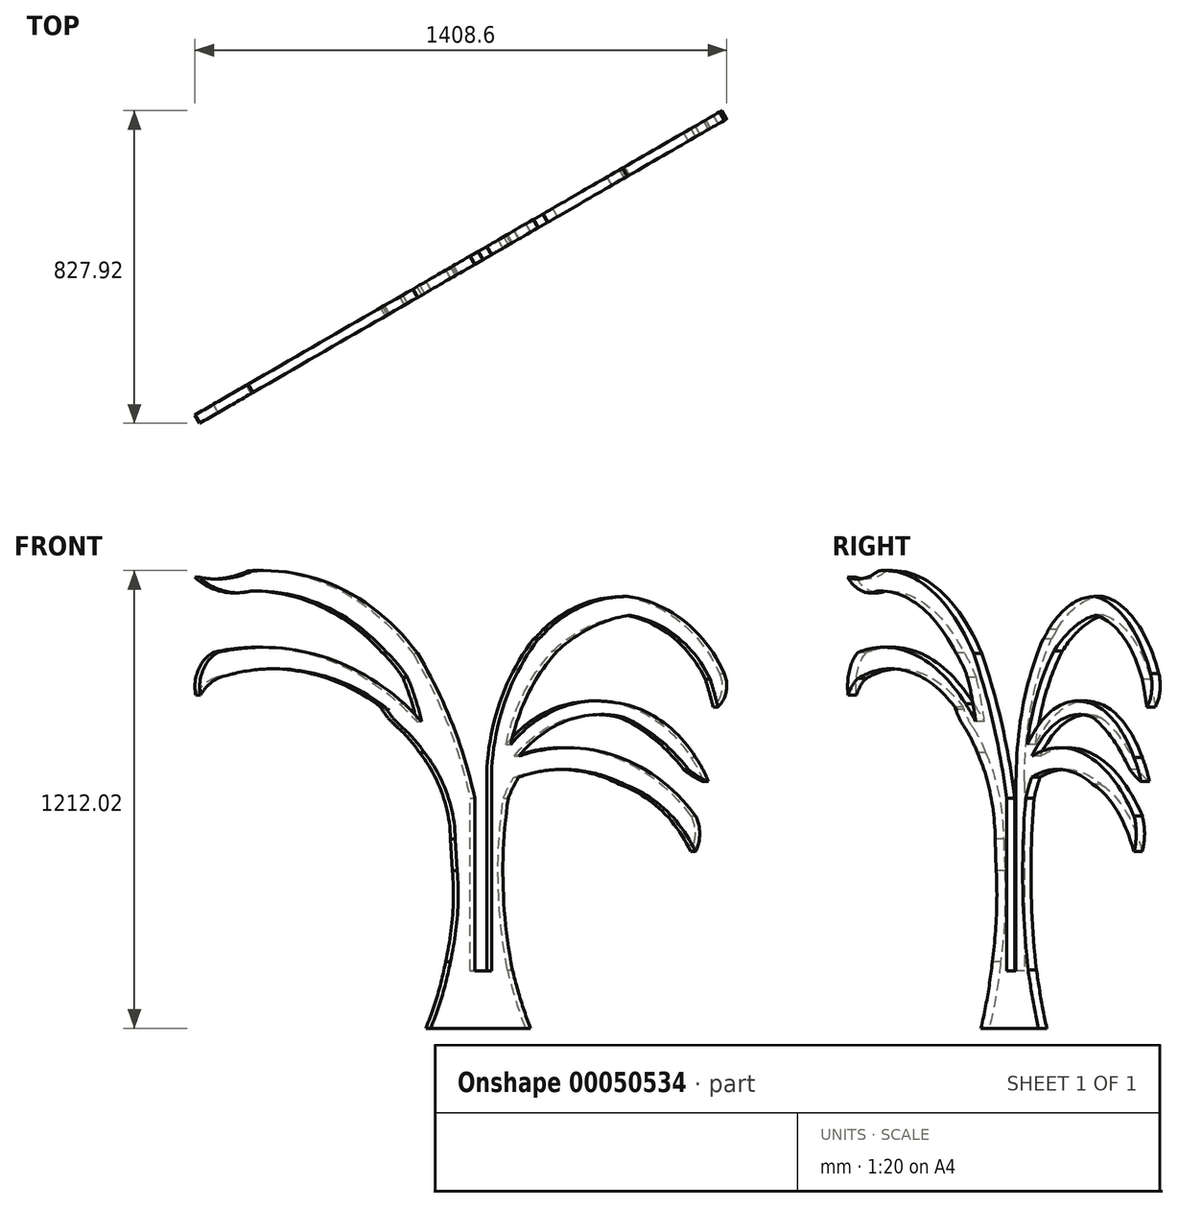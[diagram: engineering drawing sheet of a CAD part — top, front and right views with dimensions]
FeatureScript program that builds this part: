
annotation { "Feature Type Name" : "Feature", "Feature Type Description" : "" }
export const myFeature = defineFeature(function(context is Context, id is Id, definition is map)
    precondition{}
    {
        {
            var Q0;
            Q0=qCreatedBy(makeId("Front.planeOp"),FACE);
            var sketch = newSketch(context, id + "F0", { "sketchPlane" : qUnion([Q0])});
            skLineSegment(sketch, "E0", {"start": v(290.3, 214.33) * mm, "end": v(290.72, 214.4) * mm});
            skArc(sketch, "E1", {"start": v(291.68, 214.42) * mm, "mid": v(291, 214.37) * mm, "end": v(290.3, 214.33) * mm});
            skArc(sketch, "E2", {"start": v(250.18, 167.25) * mm, "mid": v(213.74, 135.77) * mm, "end": v(182.02, 99.53) * mm});
            skArc(sketch, "E3", {"start": v(290.72, 214.4) * mm, "mid": v(290.52, 214.37) * mm, "end": v(290.31, 214.33) * mm});
            skLineSegment(sketch, "E4", {"start": v(-55.85, -81.88) * mm, "end": v(-55.85, -83.32) * mm});
            skPoint(sketch, "E5.start.orphan", {"position": v(-34.4, -113.68) * mm});
            skPoint(sketch, "E6.orphan", {"position": v(111.38, -113.68) * mm});
            skArc(sketch, "E7", {"start": v(250.18, 167.25) * mm, "mid": v(278.11, 191.89) * mm, "end": v(301.41, 220.94) * mm});
            skPoint(sketch, "E8.orphan", {"position": v(-55.85, -232.39) * mm});
            skLineSegment(sketch, "E9", {"start": v(-141.99, -629.95) * mm, "end": v(162.81, -629.95) * mm});
            skPoint(sketch, "E10.orphan", {"position": v(-55.85, -157.13) * mm});
            skArc(sketch, "E11", {"start": v(-74.5, -20.43) * mm, "mid": v(-89.07, 7.78) * mm, "end": v(-106.03, 34.63) * mm});
            skArc(sketch, "E12", {"start": v(-141.99, -629.95) * mm, "mid": v(-111.9, -553.39) * mm, "end": v(-87.05, -474.97) * mm});
            skArc(sketch, "E13", {"start": v(102.75, -454.33) * mm, "mid": v(127.69, -543.88) * mm, "end": v(162.81, -629.95) * mm});
            skLineSegment(sketch, "E14", {"start": v(2.27, -477.57) * mm, "end": v(27.67, -477.57) * mm});
            skLineSegment(sketch, "E15", {"start": v(27.67, -477.57) * mm, "end": v(27.67, -20.37) * mm});
            skLineSegment(sketch, "E16", {"start": v(-23.12, -20.37) * mm, "end": v(-23.12, -478.3) * mm});
            skLineSegment(sketch, "E17", {"start": v(-23.12, -478.3) * mm, "end": v(2.27, -477.57) * mm});
            skPoint(sketch, "E18.endSnap0", {"position": v(14.97, -477.57) * mm});
            skLineSegment(sketch, "E19", {"start": v(-23.12, -20.37) * mm, "end": v(-23.12, 23.72) * mm});
            skPoint(sketch, "E20.end.orphan", {"position": v(2.27, -20.37) * mm});
            skPoint(sketch, "E21.end.orphan", {"position": v(2.27, -17.3) * mm});
            skArc(sketch, "E22", {"start": v(-87.05, -474.97) * mm, "mid": v(-58.45, -248.32) * mm, "end": v(-74.5, -20.43) * mm});
            skPoint(sketch, "E23.orphan", {"position": v(-44.84, -232.39) * mm});
            skArc(sketch, "E24", {"start": v(81.3, -213) * mm, "mid": v(81.3, -334.61) * mm, "end": v(102.75, -454.33) * mm});
            skArc(sketch, "E25", {"start": v(182.02, 99.53) * mm, "mid": v(113.83, -6.25) * mm, "end": v(87.04, -129.23) * mm});
            skLineSegment(sketch, "E26", {"start": v(88.63, -106.02) * mm, "end": v(79.4, -240.82) * mm});
            skArc(sketch, "E27", {"start": v(-107.67, 90.81) * mm, "mid": v(-255.14, 185.05) * mm, "end": v(-429.96, 193.07) * mm});
            skArc(sketch, "E28", {"start": v(-82.28, 121.03) * mm, "mid": v(-222.9, 214.74) * mm, "end": v(-390.8, 233.8) * mm});
            skPoint(sketch, "E29.orphan", {"position": v(94.7, 348.12) * mm});
            skPoint(sketch, "E30.orphan", {"position": v(94.7, 409.56) * mm});
            skArc(sketch, "E31", {"start": v(268.5, 247.86) * mm, "mid": v(255.17, 239.57) * mm, "end": v(243.48, 229.1) * mm});
            skArc(sketch, "E32", {"start": v(243.48, 229.1) * mm, "mid": v(216.85, 206.4) * mm, "end": v(191.04, 182.75) * mm});
            skArc(sketch, "E33", {"start": v(202.76, 362.22) * mm, "mid": v(199.88, 358.1) * mm, "end": v(197.05, 353.95) * mm});
            skArc(sketch, "E34", {"start": v(295.16, 363.78) * mm, "mid": v(301.5, 369.1) * mm, "end": v(307.13, 375.15) * mm});
            skArc(sketch, "E35", {"start": v(295.16, 363.78) * mm, "mid": v(262.56, 333.64) * mm, "end": v(234.09, 299.57) * mm});
            skArc(sketch, "E36", {"start": v(234.09, 299.57) * mm, "mid": v(209.24, 242.39) * mm, "end": v(191.04, 182.75) * mm});
            skArc(sketch, "E37", {"start": v(-23.12, 23.72) * mm, "mid": v(-60.17, 225.13) * mm, "end": v(-166.48, 400.18) * mm});
            skArc(sketch, "E38", {"start": v(-195.11, 426.04) * mm, "mid": v(-181.5, 412.34) * mm, "end": v(-166.48, 400.18) * mm});
            skArc(sketch, "E39", {"start": v(-82.28, 121.03) * mm, "mid": v(-135.46, 255.2) * mm, "end": v(-224.55, 368.72) * mm});
            skArc(sketch, "E40", {"start": v(706.33, 581.23) * mm, "mid": v(428.76, 531) * mm, "end": v(202.76, 362.22) * mm});
            skArc(sketch, "E41", {"start": v(712.74, 527.8) * mm, "mid": v(487.33, 488.11) * mm, "end": v(295.16, 363.78) * mm});
            skArc(sketch, "E42", {"start": v(712.74, 527.8) * mm, "mid": v(794.93, 528) * mm, "end": v(868.76, 564.14) * mm});
            skArc(sketch, "E43", {"start": v(706.33, 581.23) * mm, "mid": v(786.33, 561.13) * mm, "end": v(868.76, 564.14) * mm});
            skArc(sketch, "E44", {"start": v(813.2, 365.36) * mm, "mid": v(513.41, 359.63) * mm, "end": v(243.48, 229.1) * mm});
            skArc(sketch, "E45", {"start": v(813.2, 296.97) * mm, "mid": v(543.14, 314.4) * mm, "end": v(291.68, 214.42) * mm});
            skArc(sketch, "E46", {"start": v(866.63, 252.08) * mm, "mid": v(843.24, 278.49) * mm, "end": v(813.2, 296.97) * mm});
            skArc(sketch, "E47", {"start": v(866.63, 252.08) * mm, "mid": v(859.29, 317.86) * mm, "end": v(813.2, 365.36) * mm});
            skArc(sketch, "E48", {"start": v(-107.67, 90.81) * mm, "mid": v(-400.9, 91.96) * mm, "end": v(-647.16, -67.23) * mm});
            skArc(sketch, "E49", {"start": v(-106.03, 34.63) * mm, "mid": v(-268.96, 54.73) * mm, "end": v(-428.58, 16.4) * mm});
            skArc(sketch, "E50", {"start": v(-647.16, -67.23) * mm, "mid": v(-660.05, -114.54) * mm, "end": v(-647.16, -161.85) * mm});
            skArc(sketch, "E51", {"start": v(-428.58, 16.4) * mm, "mid": v(-555.3, -51.34) * mm, "end": v(-647.16, -161.85) * mm});
            skPoint(sketch, "E52.orphan", {"position": v(-325.64, 0) * mm});
            skPoint(sketch, "E53.endSnap0", {"position": v(-268.96, 54.73) * mm});
            skPoint(sketch, "E53.end.orphan", {"position": v(-625.65, 54.73) * mm});
            skArc(sketch, "E54", {"start": v(-429.96, 193.07) * mm, "mid": v(-535.94, 135.4) * mm, "end": v(-625.65, 54.73) * mm});
            skArc(sketch, "E55", {"start": v(-390.8, 233.8) * mm, "mid": v(-534.85, 188.53) * mm, "end": v(-647.16, 87.6) * mm});
            skArc(sketch, "E56", {"start": v(-647.16, 87.6) * mm, "mid": v(-668.75, 56.7) * mm, "end": v(-685.86, 23.1) * mm});
            skArc(sketch, "E57", {"start": v(-685.86, 23.1) * mm, "mid": v(-654.78, 37.05) * mm, "end": v(-625.65, 54.73) * mm});
            skArc(sketch, "E58", {"start": v(-224.55, 368.72) * mm, "mid": v(-328.36, 431.2) * mm, "end": v(-445.02, 463.93) * mm});
            skArc(sketch, "E59", {"start": v(-166.48, 400.18) * mm, "mid": v(-291.34, 483.65) * mm, "end": v(-438.57, 513.39) * mm});
            skArc(sketch, "E60", {"start": v(-445.02, 463.93) * mm, "mid": v(-588.64, 408.05) * mm, "end": v(-692.32, 294.04) * mm});
            skArc(sketch, "E61", {"start": v(-438.57, 513.39) * mm, "mid": v(-612.47, 448.32) * mm, "end": v(-735.32, 309.1) * mm});
            skArc(sketch, "E62", {"start": v(-735.32, 309.1) * mm, "mid": v(-741.11, 261.62) * mm, "end": v(-715.97, 220.93) * mm});
            skArc(sketch, "E63", {"start": v(-692.32, 294.04) * mm, "mid": v(-704.49, 257.6) * mm, "end": v(-715.97, 220.93) * mm});
            skArc(sketch, "E64", {"start": v(202.76, 362.22) * mm, "mid": v(97.96, 178.82) * mm, "end": v(27.67, -20.37) * mm});
            skSolve(sketch);
        }
        {
            var Q0;
            {var subQ10=sQuery(id+"F0.wireOp",EDGE,"E0");Q0=makeQuery(id+"F0.imprint","IMPRINT",FACE,{"disambiguationData":[TD([[makeQuery(id+"F0.imprint","IMPRINT",EDGE,{"derivedFrom":subQ10}),1.0]])]});}
            extrude(context, id + "F1", {"entities" : qUnion([Q0]), "depth" : 25.4 * mm});
        }
        {
            var Q0;
            Q0=makeQuery(id+"F1.opExtrude","SWEPT_BODY",BODY,{"disambiguationData":[OSD([sQuery(id+"F0.wireOp",EDGE,"E0"),sQuery(id+"F0.wireOp",EDGE,"E1"),sQuery(id+"F0.wireOp",EDGE,"E2"),sQuery(id+"F0.wireOp",EDGE,"E3"),sQuery(id+"F0.wireOp",EDGE,"d9638828-1f17-4b2b-8995-5361523860e0"),sQuery(id+"F0.wireOp",EDGE,"ca680470-7f5b-4d99-8480-94b26c12f4fd"),sQuery(id+"F0.wireOp",EDGE,"de8b8b54-e7c7-4b21-ae84-d369e1465e8a"),sQuery(id+"F0.wireOp",EDGE,"c37bc43b-cfe4-44e1-a1ae-5abd4e94952b"),sQuery(id+"F0.wireOp",EDGE,"23d1508a-aa4c-4ded-80db-4c8a4c75fcde"),sQuery(id+"F0.wireOp",EDGE,"E7"),sQuery(id+"F0.wireOp",EDGE,"E9"),sQuery(id+"F0.wireOp",EDGE,"E11"),sQuery(id+"F0.wireOp",EDGE,"E12"),sQuery(id+"F0.wireOp",EDGE,"E13"),sQuery(id+"F0.wireOp",EDGE,"E14"),sQuery(id+"F0.wireOp",EDGE,"E15"),sQuery(id+"F0.wireOp",EDGE,"E16"),sQuery(id+"F0.wireOp",EDGE,"E17"),sQuery(id+"F0.wireOp",EDGE,"E19"),sQuery(id+"F0.wireOp",EDGE,"137eaf7c-178d-4598-95e7-84a11a8a7aad"),sQuery(id+"F0.wireOp",EDGE,"E22"),sQuery(id+"F0.wireOp",EDGE,"E24"),sQuery(id+"F0.wireOp",EDGE,"E25"),sQuery(id+"F0.wireOp",EDGE,"E26")])]});
            var Q1;
            Q1=makeQuery(id+"F1.opExtrude","CAP_EDGE",EDGE,{"disambiguationData":[OSD([sQuery(id+"F0.wireOp",EDGE,"E15"),sQuery(id+"F0.wireOp",EDGE,"137eaf7c-178d-4598-95e7-84a11a8a7aad")])],"isStart":false});
            transform(context, id + "F2", {"entities" : qUnion([Q0]), "transformType" : TransformType.ROTATION, "transformAxis" : qUnion([Q1]), "angle" : 240 * degree, "makeCopy" : false});
        }
        {
            var Q0;
            Q0=makeQuery(id+"F1.opExtrude","SWEPT_BODY",BODY,{"disambiguationData":[OSD([sQuery(id+"F0.wireOp",EDGE,"E0"),sQuery(id+"F0.wireOp",EDGE,"E1"),sQuery(id+"F0.wireOp",EDGE,"E2"),sQuery(id+"F0.wireOp",EDGE,"E3"),sQuery(id+"F0.wireOp",EDGE,"d9638828-1f17-4b2b-8995-5361523860e0"),sQuery(id+"F0.wireOp",EDGE,"ca680470-7f5b-4d99-8480-94b26c12f4fd"),sQuery(id+"F0.wireOp",EDGE,"de8b8b54-e7c7-4b21-ae84-d369e1465e8a"),sQuery(id+"F0.wireOp",EDGE,"c37bc43b-cfe4-44e1-a1ae-5abd4e94952b"),sQuery(id+"F0.wireOp",EDGE,"23d1508a-aa4c-4ded-80db-4c8a4c75fcde"),sQuery(id+"F0.wireOp",EDGE,"E7"),sQuery(id+"F0.wireOp",EDGE,"E9"),sQuery(id+"F0.wireOp",EDGE,"E11"),sQuery(id+"F0.wireOp",EDGE,"E12"),sQuery(id+"F0.wireOp",EDGE,"E13"),sQuery(id+"F0.wireOp",EDGE,"E14"),sQuery(id+"F0.wireOp",EDGE,"E15"),sQuery(id+"F0.wireOp",EDGE,"E16"),sQuery(id+"F0.wireOp",EDGE,"E17"),sQuery(id+"F0.wireOp",EDGE,"E19"),sQuery(id+"F0.wireOp",EDGE,"137eaf7c-178d-4598-95e7-84a11a8a7aad"),sQuery(id+"F0.wireOp",EDGE,"E22"),sQuery(id+"F0.wireOp",EDGE,"E24"),sQuery(id+"F0.wireOp",EDGE,"E25"),sQuery(id+"F0.wireOp",EDGE,"E26")])]});
            var Q1;
            Q1=makeQuery(id+"F1.opExtrude","CAP_EDGE",EDGE,{"disambiguationData":[OSD([sQuery(id+"F0.wireOp",EDGE,"E16"),sQuery(id+"F0.wireOp",EDGE,"E19")])],"isStart":true});
            transform(context, id + "F3", {"entities" : qUnion([Q0]), "transformType" : TransformType.ROTATION, "transformAxis" : qUnion([Q1]), "angle" : 30 * degree, "makeCopy" : false});
        }
    });
